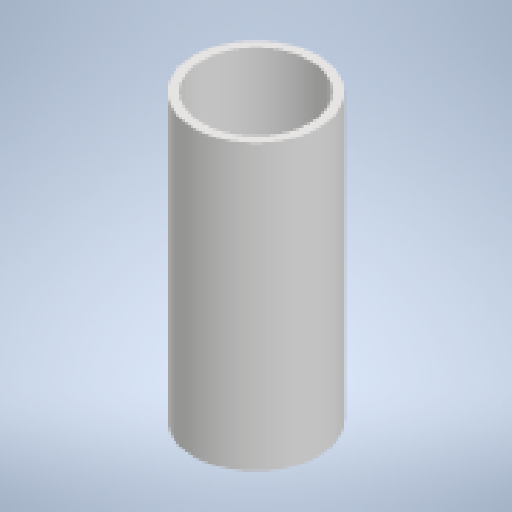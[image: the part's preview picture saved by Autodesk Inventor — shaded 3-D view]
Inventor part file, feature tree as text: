
AUTODESK INVENTOR PART (.ipt)
format: ipt  version: 2025 (Build 290162010, 162A)  size: 224,256 bytes
history: native  units: mm
features: extrude x1, sketch x1
ambient origin geometry x8: Origin, YZ Plane, XZ Plane, XY Plane, X Axis, Y Axis, Z Axis, Center Point
bodies: Solid1 (feature_tree)
feature tree (2):
  extrude  "Extrusion1"  Depth=203.2mm
  sketch  "Sketch1"  dims[d0=89.6mm d1=77.3mm d2=203.2mm d3=0.0mm]
